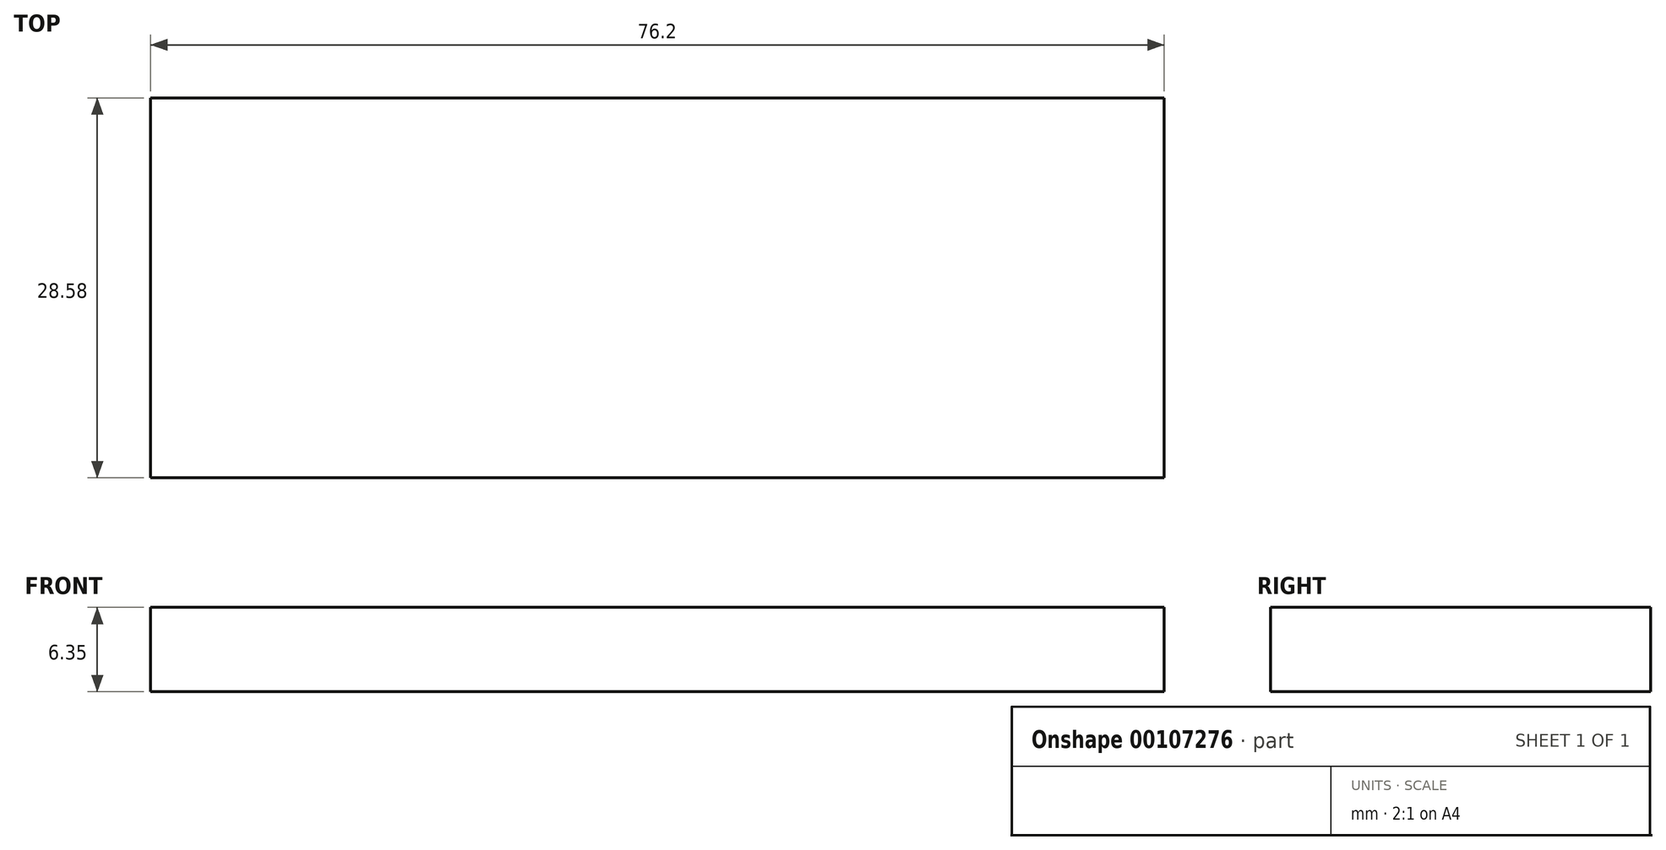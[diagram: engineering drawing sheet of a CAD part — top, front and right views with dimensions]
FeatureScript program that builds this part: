
annotation { "Feature Type Name" : "Feature", "Feature Type Description" : "" }
export const myFeature = defineFeature(function(context is Context, id is Id, definition is map)
    precondition{}
    {
        {
            var Q0;
            Q0=qCreatedBy(makeId("Top.planeOp"),FACE);
            var sketch = newSketch(context, id + "F0", { "sketchPlane" : qUnion([Q0])});
            skLineSegment(sketch, "E0.bottom", {"start": v(38.1, -14.29) * mm, "end": v(-38.1, -14.29) * mm});
            skLineSegment(sketch, "E0.top", {"start": v(38.1, 14.29) * mm, "end": v(-38.1, 14.29) * mm});
            skLineSegment(sketch, "E0.left", {"start": v(38.1, -14.29) * mm, "end": v(38.1, 14.29) * mm});
            skLineSegment(sketch, "E0.right", {"start": v(-38.1, -14.29) * mm, "end": v(-38.1, 14.29) * mm});
            skPoint(sketch, "E0.middle", {"position": v(0, 0) * mm});
            skSolve(sketch);
        }
        {
            var Q0;
            Q0=qSketchRegion(id+"F0",true);
            extrude(context, id + "F1", {"entities" : qUnion([Q0]), "depth" : 6.35 * mm});
        }
    });
